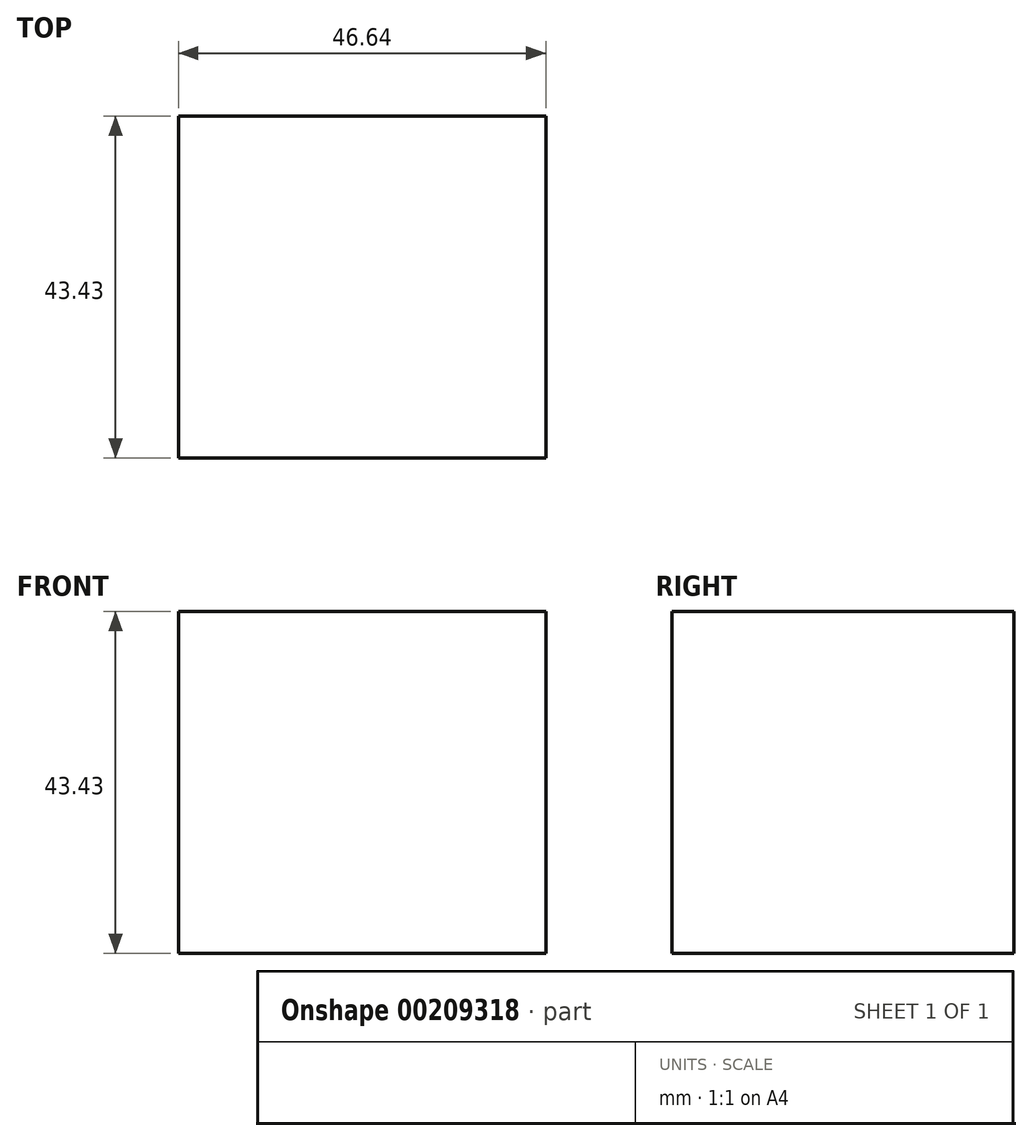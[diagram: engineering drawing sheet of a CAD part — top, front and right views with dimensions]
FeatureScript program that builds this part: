
annotation { "Feature Type Name" : "Feature", "Feature Type Description" : "" }
export const myFeature = defineFeature(function(context is Context, id is Id, definition is map)
    precondition{}
    {
        {
            var Q0;
            Q0=qCreatedBy(makeId("Top.planeOp"),FACE);
            var sketch = newSketch(context, id + "F0", { "sketchPlane" : qUnion([Q0])});
            skLineSegment(sketch, "E0.bottom", {"start": v(-23.03, 21.42) * mm, "end": v(23.6, 21.42) * mm});
            skLineSegment(sketch, "E0.top", {"start": v(-23.03, -22) * mm, "end": v(23.6, -22) * mm});
            skLineSegment(sketch, "E0.left", {"start": v(-23.03, 21.42) * mm, "end": v(-23.03, -22) * mm});
            skLineSegment(sketch, "E0.right", {"start": v(23.6, 21.42) * mm, "end": v(23.6, -22) * mm});
            skSolve(sketch);
        }
        {
            var Q0;
            Q0=makeQuery(id+"F0.imprint","IMPRINT",FACE,{"disambiguationData":[TD([[makeQuery(id+"F0.imprint","IMPRINT",EDGE,{"derivedFrom":sQuery(id+"F0.wireOp",EDGE,"E0.bottom")}),-1.0]])]});
            extrude(context, id + "F1", {"entities" : qUnion([Q0]), "depth" : 43.43 * mm});
        }
    });
